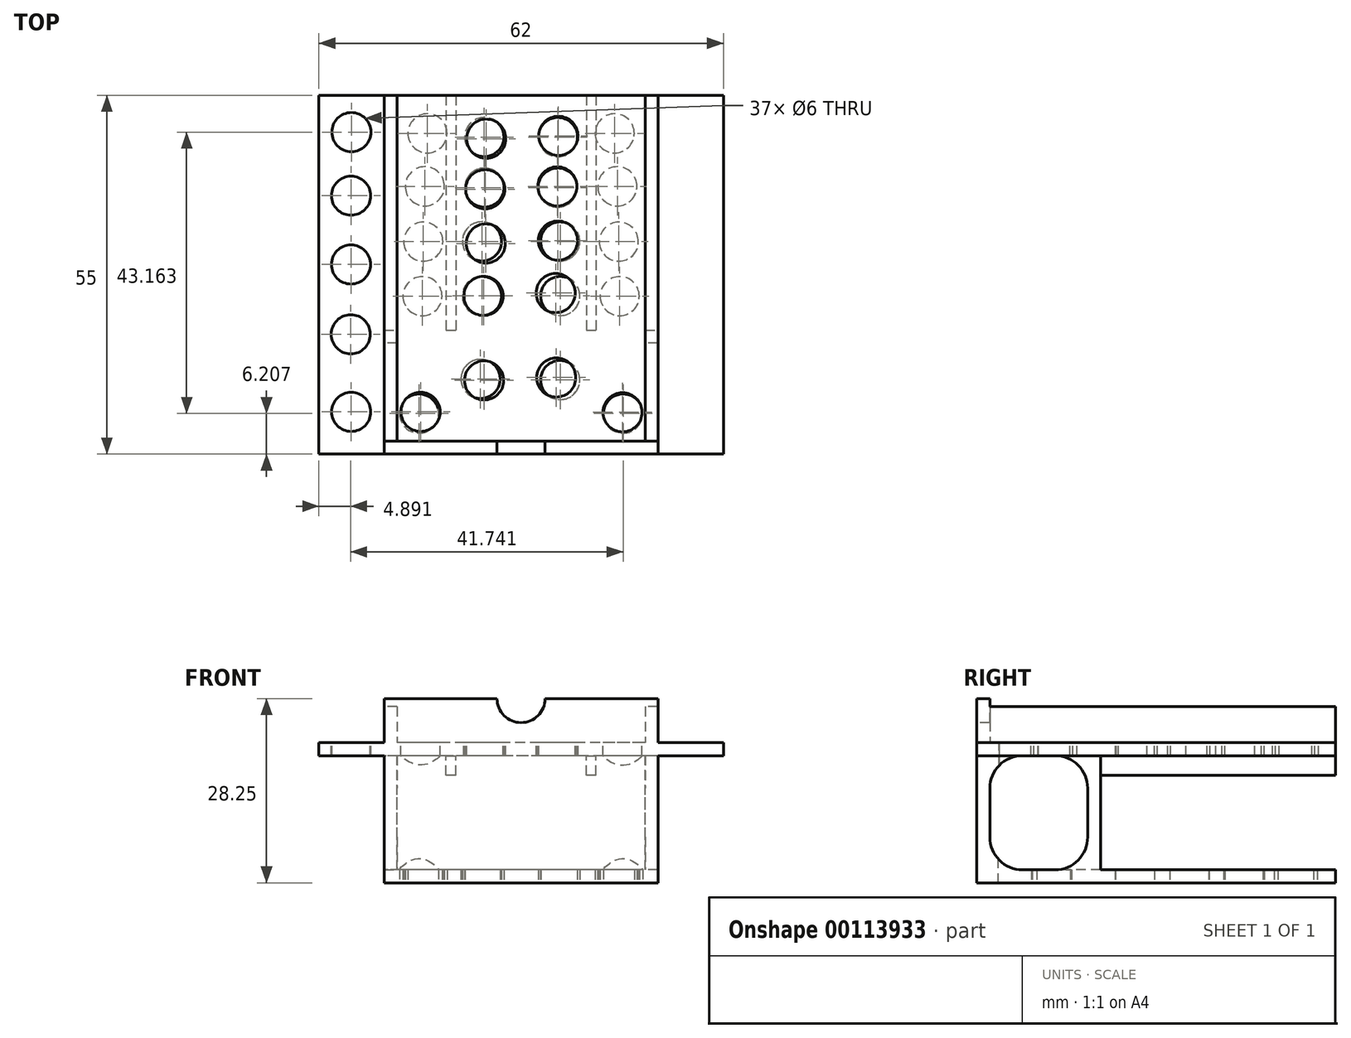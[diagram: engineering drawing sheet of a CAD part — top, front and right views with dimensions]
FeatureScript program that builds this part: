
annotation { "Feature Type Name" : "Feature", "Feature Type Description" : "" }
export const myFeature = defineFeature(function(context is Context, id is Id, definition is map)
    precondition{}
    {
        {
            var Q0;
            Q0=qCreatedBy(makeId("Front.planeOp"),FACE);
            var sketch = newSketch(context, id + "F0", { "sketchPlane" : qUnion([Q0])});
            skLineSegment(sketch, "E0.top", {"start": v(21, 17.5) * mm, "end": v(3.68, 17.5) * mm});
            skLineSegment(sketch, "E0.left", {"start": v(21, -10.75) * mm, "end": v(21, 17.5) * mm});
            skLineSegment(sketch, "E0.right", {"start": v(-21, -10.75) * mm, "end": v(-21, 17.5) * mm});
            skPoint(sketch, "E0.middle", {"position": v(0, 0) * mm});
            skLineSegment(sketch, "E1.bottom", {"start": v(21, -8.75) * mm, "end": v(-21, -8.75) * mm});
            skLineSegment(sketch, "E1.top", {"start": v(21, 8.75) * mm, "end": v(-21, 8.75) * mm});
            skLineSegment(sketch, "E1.left", {"start": v(21, -8.75) * mm, "end": v(21, 8.75) * mm});
            skLineSegment(sketch, "E1.right", {"start": v(-21, -8.75) * mm, "end": v(-21, 8.75) * mm});
            skLineSegment(sketch, "E2.bottom", {"start": v(21, -10.75) * mm, "end": v(-21, -10.75) * mm});
            skLineSegment(sketch, "E2.top", {"start": v(21, 10.75) * mm, "end": v(-21, 10.75) * mm});
            skLineSegment(sketch, "E2.left", {"start": v(21, -10.75) * mm, "end": v(21, 10.75) * mm});
            skLineSegment(sketch, "E2.right", {"start": v(-21, -10.75) * mm, "end": v(-21, 10.75) * mm});
            skArc(sketch, "E3", {"start": v(-3.68, 17.5) * mm, "mid": v(0, 13.82) * mm, "end": v(3.68, 17.5) * mm});
            skLineSegment(sketch, "E4.trimOffspring", {"start": v(-3.68, 17.5) * mm, "end": v(-21, 17.5) * mm});
            skPoint(sketch, "E5.orphan", {"position": v(-21, -17.5) * mm});
            skPoint(sketch, "E6.orphan", {"position": v(21, -17.5) * mm});
            skSolve(sketch);
        }
        {
            var Q0;
            Q0 = qSketchRegion(id + "F0", true);
            extrude(context, id + "F1", {"entities" : qUnion([Q0]), "oppositeDirection" : true, "depth" : 2 * mm});
        }
        {
            var Q0;
            {var subQ0=sQuery(id+"F0.wireOp",EDGE,"E1.top");Q0=makeQuery(id+"F0.imprint","IMPRINT",FACE,{"disambiguationData":[TD([[makeQuery(id+"F0.imprint","IMPRINT",EDGE,{"derivedFrom":subQ0}),-1.0]])]});}
            var Q1;
            {var subQ0=sQuery(id+"F0.wireOp",EDGE,"E1.bottom");Q1=makeQuery(id+"F0.imprint","IMPRINT",FACE,{"disambiguationData":[TD([[makeQuery(id+"F0.imprint","IMPRINT",EDGE,{"derivedFrom":subQ0}),1.0]])]});}
            extrude(context, id + "F2", {"entities" : qUnion([Q0, Q1]), "operationType" : NewBodyOperationType.ADD, "oppositeDirection" : true, "depth" : 55 * mm});
        }
        {
            var Q0;
            Q0=makeQuery(id+"F2.opExtrude","SWEPT_FACE",FACE,{"disambiguationData":[OSD([sQuery(id+"F0.wireOp",EDGE,"E2.top")])]});
            var sketch = newSketch(context, id + "F3", { "sketchPlane" : qUnion([Q0])});
            skLineSegment(sketch, "E7.bottom", {"start": v(21, 2) * mm, "end": v(-21, 2) * mm});
            skLineSegment(sketch, "E7.top", {"start": v(21, 17) * mm, "end": v(-21, 17) * mm});
            skLineSegment(sketch, "E7.left", {"start": v(21, 2) * mm, "end": v(21, 17) * mm});
            skLineSegment(sketch, "E7.right", {"start": v(-21, 2) * mm, "end": v(-21, 17) * mm});
            skPoint(sketch, "E7.middle", {"position": v(0, 9.5) * mm});
            skLineSegment(sketch, "E8", {"start": v(-21, 19) * mm, "end": v(21, 19) * mm});
            skLineSegment(sketch, "E9", {"start": v(0, 55) * mm, "end": v(0, 0) * mm, "construction": true});
            skLineSegment(sketch, "E10", {"start": v(-19, 55) * mm, "end": v(-19, 19) * mm});
            skLineSegment(sketch, "E11.MirrorCS", {"start": v(19, 55) * mm, "end": v(19, 19) * mm});
            skLineSegment(sketch, "E12", {"start": v(-19, 19) * mm, "end": v(-19, 2) * mm});
            skLineSegment(sketch, "E13", {"start": v(19, 19) * mm, "end": v(19, 2) * mm});
            skLineSegment(sketch, "E14.bottom", {"start": v(-11.49, 55) * mm, "end": v(-9.99, 55) * mm});
            skLineSegment(sketch, "E14.top", {"start": v(-11.49, 19) * mm, "end": v(-9.99, 19) * mm});
            skLineSegment(sketch, "E14.left", {"start": v(-11.49, 55) * mm, "end": v(-11.49, 19) * mm});
            skLineSegment(sketch, "E14.right", {"start": v(-9.99, 55) * mm, "end": v(-9.99, 19) * mm});
            skLineSegment(sketch, "E15.MirrorCS", {"start": v(9.99, 55) * mm, "end": v(9.99, 19) * mm});
            skLineSegment(sketch, "E16.MirrorCS", {"start": v(11.49, 55) * mm, "end": v(11.49, 19) * mm});
            skSolve(sketch);
        }
        {
            var Q0;
            {var subQ0=sQuery(id+"F3.wireOp",EDGE,"E7.top");Q0=makeQuery(id+"F3.imprint","IMPRINT",FACE,{"disambiguationData":[TD([[makeQuery(id+"F3.imprint","IMPRINT",EDGE,{"derivedFrom":subQ0}),-1.0]])]});}
            var Q1;
            {var subQ0=sQuery(id+"F3.wireOp",EDGE,"E14.top");Q1=makeQuery(id+"F3.imprint","IMPRINT",FACE,{"disambiguationData":[TD([[makeQuery(id+"F3.imprint","IMPRINT",EDGE,{"derivedFrom":subQ0}),-1.0]])]});}
            extrude(context, id + "F4", {"entities" : qUnion([Q0, Q1]), "operationType" : NewBodyOperationType.ADD, "oppositeDirection" : true, "depth" : 21.48 * mm});
        }
        {
            var Q0;
            {var subQ0=sQuery(id+"F3.wireOp",EDGE,"E7.left");Q0=makeQuery(id+"F3.imprint","IMPRINT",FACE,{"disambiguationData":[TD([[makeQuery(id+"F3.imprint","IMPRINT",EDGE,{"derivedFrom":subQ0}),-1.0]])]});}
            var Q1;
            {var subQ0=sQuery(id+"F3.wireOp",EDGE,"E7.top");var subQ3=sQuery(id+"F3.wireOp",EDGE,"E13");var subQ4=makeQuery(id+"F3.imprint","INTERSECT",VERTEX,{"derivedFrom":[subQ0,subQ3]});Q1=makeQuery(id+"F3.imprint","IMPRINT",FACE,{"disambiguationData":[TD([[makeQuery(id+"F3.imprint","IMPRINT",EDGE,{"disambiguationData":[TD([[subQ4,1.0]])],"derivedFrom":subQ3}),1.0]])]});}
            var Q2;
            {var subQ4=sQuery(id+"F3.wireOp",EDGE,"E11.MirrorCS");Q2=makeQuery(id+"F3.imprint","IMPRINT",FACE,{"disambiguationData":[TD([[makeQuery(id+"F3.imprint","IMPRINT",EDGE,{"derivedFrom":subQ4}),1.0]])]});}
            var Q3;
            {var subQ0=sQuery(id+"F3.wireOp",EDGE,"E7.top");var subQ3=sQuery(id+"F3.wireOp",EDGE,"E12");var subQ4=makeQuery(id+"F3.imprint","INTERSECT",VERTEX,{"derivedFrom":[subQ0,subQ3]});Q3=makeQuery(id+"F3.imprint","IMPRINT",FACE,{"disambiguationData":[TD([[makeQuery(id+"F3.imprint","IMPRINT",EDGE,{"disambiguationData":[TD([[subQ4,1.0]])],"derivedFrom":subQ3}),-1.0]])]});}
            var Q4;
            {var subQ4=sQuery(id+"F3.wireOp",EDGE,"E10");Q4=makeQuery(id+"F3.imprint","IMPRINT",FACE,{"disambiguationData":[TD([[makeQuery(id+"F3.imprint","IMPRINT",EDGE,{"derivedFrom":subQ4}),-1.0]])]});}
            var Q5;
            {var subQ0=sQuery(id+"F3.wireOp",EDGE,"E7.right");Q5=makeQuery(id+"F3.imprint","IMPRINT",FACE,{"disambiguationData":[TD([[makeQuery(id+"F3.imprint","IMPRINT",EDGE,{"derivedFrom":subQ0}),1.0]])]});}
            extrude(context, id + "F5", {"entities" : qUnion([Q0, Q1, Q2, Q3, Q4, Q5]), "operationType" : NewBodyOperationType.ADD, "depth" : 5.5 * mm});
        }
        {
            var Q0;
            Q0=makeQuery(id+"F3.imprint","IMPRINT",FACE,{"disambiguationData":[TD([[makeQuery(id+"F3.imprint","IMPRINT",EDGE,{"derivedFrom":sQuery(id+"F3.wireOp",EDGE,"E14.bottom")}),1.0]])]});
            var Q1;
            {var subQ0=sQuery(id+"F3.wireOp",EDGE,"E15.MirrorCS");Q1=makeQuery(id+"F3.imprint","IMPRINT",FACE,{"disambiguationData":[TD([[makeQuery(id+"F3.imprint","IMPRINT",EDGE,{"derivedFrom":subQ0}),1.0]])]});}
            extrude(context, id + "F6", {"entities" : qUnion([Q0, Q1]), "operationType" : NewBodyOperationType.ADD, "oppositeDirection" : true, "depth" : 5 * mm});
        }
        {
            var Q0;
            {var subQ0=sQuery(id+"F0.wireOp",EDGE,"E2.left");var subQ1=sQuery(id+"F0.wireOp",EDGE,"E2.top");var subQ2=sQuery(id+"F0.wireOp",EDGE,"E0.left");Q0=makeQuery(id+"F5.boolean.opBoolean","MERGE",FACE,{"derivedFrom":[makeQuery(id+"F4.boolean.opBoolean","MERGE",FACE,{"derivedFrom":[makeQuery(id+"F2.boolean.opBoolean","MERGE",FACE,{"derivedFrom":[makeQuery(id+"F1.opExtrude","SWEPT_FACE",FACE,{"disambiguationData":[OSD([subQ2,subQ0])]}),makeQuery(id+"F2.opExtrude","SWEPT_FACE",FACE,{"disambiguationData":[OSD([subQ0]),TDD([makeQuery(id+"F0.imprint","IMPRINT",EDGE,{"disambiguationData":[TD([[makeQuery(id+"F0.imprint","INTERSECT",VERTEX,{"derivedFrom":[sQuery(id+"F0.wireOp",EDGE,"E1.bottom"),subQ0]}),1.0]])],"derivedFrom":subQ0})])]}),makeQuery(id+"F2.opExtrude","SWEPT_FACE",FACE,{"disambiguationData":[OSD([subQ0]),TDD([makeQuery(id+"F0.imprint","IMPRINT",EDGE,{"disambiguationData":[TD([[makeQuery(id+"F0.imprint","INTERSECT",VERTEX,{"derivedFrom":[sQuery(id+"F0.wireOp",EDGE,"E1.top"),subQ0]}),-1.0]])],"derivedFrom":subQ0})])]})]}),makeQuery(id+"F4.opExtrude","SWEPT_FACE",FACE,{"disambiguationData":[OSD([subQ2,subQ1,subQ0])]})]}),makeQuery(id+"F5.opExtrude","SWEPT_FACE",FACE,{"disambiguationData":[OSD([subQ2,subQ1,subQ0,sQuery(id+"F3.wireOp",EDGE,"E7.left")])]})]});}
            var sketch = newSketch(context, id + "F7", { "sketchPlane" : qUnion([Q0])});
            skLineSegment(sketch, "E17", {"start": v(55, 8.75) * mm, "end": v(0, 8.75) * mm});
            skPoint(sketch, "E17.endSnap0", {"position": v(9.5, 8.75) * mm});
            skLineSegment(sketch, "E18", {"start": v(0, 8.75) * mm, "end": v(0, 11) * mm});
            skLineSegment(sketch, "E19", {"start": v(55, 8.75) * mm, "end": v(0.94, 8.75) * mm});
            skLineSegment(sketch, "E20", {"start": v(55, 10.75) * mm, "end": v(0, 10.75) * mm});
            skLineSegment(sketch, "E21", {"start": v(0, 10.75) * mm, "end": v(0, 8.75) * mm});
            skLineSegment(sketch, "E22", {"start": v(55, 8.75) * mm, "end": v(55, 10.75) * mm});
            skSolve(sketch);
        }
        {
            var Q0;
            {var subQ7=sQuery(id+"F7.wireOp",EDGE,"E17");Q0=makeQuery(id+"F7.imprint","IMPRINT",FACE,{"disambiguationData":[TD([[makeQuery(id+"F7.imprint","IMPRINT",EDGE,{"derivedFrom":subQ7}),-1.0]])]});}
            extrude(context, id + "F8", {"entities" : qUnion([Q0]), "operationType" : NewBodyOperationType.ADD, "depth" : 10 * mm});
        }
        {
            var Q0;
            {var subQ0=sQuery(id+"F0.wireOp",EDGE,"E2.right");var subQ1=sQuery(id+"F0.wireOp",EDGE,"E2.top");var subQ2=sQuery(id+"F0.wireOp",EDGE,"E0.right");Q0=makeQuery(id+"F5.boolean.opBoolean","MERGE",FACE,{"derivedFrom":[makeQuery(id+"F4.boolean.opBoolean","MERGE",FACE,{"derivedFrom":[makeQuery(id+"F2.boolean.opBoolean","MERGE",FACE,{"derivedFrom":[makeQuery(id+"F1.opExtrude","SWEPT_FACE",FACE,{"disambiguationData":[OSD([subQ2,subQ0])]}),makeQuery(id+"F2.opExtrude","SWEPT_FACE",FACE,{"disambiguationData":[OSD([subQ0]),TDD([makeQuery(id+"F0.imprint","IMPRINT",EDGE,{"disambiguationData":[TD([[makeQuery(id+"F0.imprint","INTERSECT",VERTEX,{"derivedFrom":[sQuery(id+"F0.wireOp",EDGE,"E1.bottom"),subQ0]}),1.0]])],"derivedFrom":subQ0})])]}),makeQuery(id+"F2.opExtrude","SWEPT_FACE",FACE,{"disambiguationData":[OSD([subQ0]),TDD([makeQuery(id+"F0.imprint","IMPRINT",EDGE,{"disambiguationData":[TD([[makeQuery(id+"F0.imprint","INTERSECT",VERTEX,{"derivedFrom":[sQuery(id+"F0.wireOp",EDGE,"E1.top"),subQ0]}),-1.0]])],"derivedFrom":subQ0})])]})]}),makeQuery(id+"F4.opExtrude","SWEPT_FACE",FACE,{"disambiguationData":[OSD([subQ2,subQ1,subQ0])]})]}),makeQuery(id+"F5.opExtrude","SWEPT_FACE",FACE,{"disambiguationData":[OSD([subQ2,subQ1,subQ0,sQuery(id+"F3.wireOp",EDGE,"E7.right")])]})]});}
            var sketch = newSketch(context, id + "F9", { "sketchPlane" : qUnion([Q0])});
            skLineSegment(sketch, "E23", {"start": v(0, 10.75) * mm, "end": v(-55, 10.75) * mm});
            skLineSegment(sketch, "E24", {"start": v(-55, 10.75) * mm, "end": v(-55, 8.75) * mm});
            skLineSegment(sketch, "E25", {"start": v(-55, 8.75) * mm, "end": v(0, 8.75) * mm});
            skLineSegment(sketch, "E26", {"start": v(0, 8.75) * mm, "end": v(0, 10.75) * mm});
            skSolve(sketch);
        }
        {
            var Q0;
            Q0=makeQuery(id+"F9.imprint","IMPRINT",FACE,{"disambiguationData":[TD([[makeQuery(id+"F9.imprint","IMPRINT",EDGE,{"derivedFrom":sQuery(id+"F9.wireOp",EDGE,"E23")}),1.0]])]});
            extrude(context, id + "F10", {"entities" : qUnion([Q0]), "operationType" : NewBodyOperationType.ADD, "depth" : 10 * mm});
        }
        {
            var Q0;
            Q0=makeQuery(id+"F10.opExtrude","SWEPT_FACE",FACE,{"disambiguationData":[OSD([sQuery(id+"F9.wireOp",EDGE,"E23")])]});
            var sketch = newSketch(context, id + "F11", { "sketchPlane" : qUnion([Q0])});
            skLineSegment(sketch, "E27", {"start": v(-26, 55) * mm, "end": v(-26, 0) * mm, "construction": true});
            skCircle(sketch, "E28", {"center": v(-26, 49.37) * mm, "radius": 3 * mm});
            skCircle(sketch, "E29", {"center": v(-26.06, 39.62) * mm, "radius": 3 * mm});
            skCircle(sketch, "E30", {"center": v(-26.07, 29.07) * mm, "radius": 3 * mm});
            skCircle(sketch, "E31", {"center": v(-26.1, 18.36) * mm, "radius": 3 * mm});
            skCircle(sketch, "E32", {"center": v(-26.05, 6.47) * mm, "radius": 3 * mm});
            skCircle(sketch, "E33.MirrorC", {"center": v(26.05, 6.47) * mm, "radius": 3 * mm});
            skCircle(sketch, "E34.MirrorC", {"center": v(26.1, 18.36) * mm, "radius": 3 * mm});
            skCircle(sketch, "E35.MirrorC", {"center": v(26.07, 29.07) * mm, "radius": 3 * mm});
            skCircle(sketch, "E36.MirrorC", {"center": v(26.06, 39.62) * mm, "radius": 3 * mm});
            skCircle(sketch, "E37.MirrorC", {"center": v(26, 49.37) * mm, "radius": 3 * mm});
            skSolve(sketch);
        }
        {
            var Q0;
            Q0=makeQuery(id+"F11.imprint","IMPRINT",FACE,{"disambiguationData":[TD([[makeQuery(id+"F11.imprint","IMPRINT",EDGE,{"derivedFrom":sQuery(id+"F11.wireOp",EDGE,"E33.MirrorC")}),-1.0]])]});
            var Q1;
            Q1=makeQuery(id+"F11.imprint","IMPRINT",FACE,{"disambiguationData":[TD([[makeQuery(id+"F11.imprint","IMPRINT",EDGE,{"derivedFrom":sQuery(id+"F11.wireOp",EDGE,"E34.MirrorC")}),-1.0]])]});
            var Q2;
            Q2=makeQuery(id+"F11.imprint","IMPRINT",FACE,{"disambiguationData":[TD([[makeQuery(id+"F11.imprint","IMPRINT",EDGE,{"derivedFrom":sQuery(id+"F11.wireOp",EDGE,"E35.MirrorC")}),-1.0]])]});
            var Q3;
            Q3=makeQuery(id+"F11.imprint","IMPRINT",FACE,{"disambiguationData":[TD([[makeQuery(id+"F11.imprint","IMPRINT",EDGE,{"derivedFrom":sQuery(id+"F11.wireOp",EDGE,"E36.MirrorC")}),-1.0]])]});
            var Q4;
            Q4=makeQuery(id+"F11.imprint","IMPRINT",FACE,{"disambiguationData":[TD([[makeQuery(id+"F11.imprint","IMPRINT",EDGE,{"derivedFrom":sQuery(id+"F11.wireOp",EDGE,"E37.MirrorC")}),-1.0]])]});
            var Q5;
            Q5=makeQuery(id+"F11.imprint","IMPRINT",FACE,{"disambiguationData":[TD([[makeQuery(id+"F11.imprint","IMPRINT",EDGE,{"derivedFrom":sQuery(id+"F11.wireOp",EDGE,"E28")}),1.0]])]});
            var Q6;
            Q6=makeQuery(id+"F11.imprint","IMPRINT",FACE,{"disambiguationData":[TD([[makeQuery(id+"F11.imprint","IMPRINT",EDGE,{"derivedFrom":sQuery(id+"F11.wireOp",EDGE,"E32")}),1.0]])]});
            var Q7;
            Q7=makeQuery(id+"F11.imprint","IMPRINT",FACE,{"disambiguationData":[TD([[makeQuery(id+"F11.imprint","IMPRINT",EDGE,{"derivedFrom":sQuery(id+"F11.wireOp",EDGE,"E31")}),1.0]])]});
            var Q8;
            Q8=makeQuery(id+"F11.imprint","IMPRINT",FACE,{"disambiguationData":[TD([[makeQuery(id+"F11.imprint","IMPRINT",EDGE,{"derivedFrom":sQuery(id+"F11.wireOp",EDGE,"E30")}),1.0]])]});
            var Q9;
            Q9=makeQuery(id+"F11.imprint","IMPRINT",FACE,{"disambiguationData":[TD([[makeQuery(id+"F11.imprint","IMPRINT",EDGE,{"derivedFrom":sQuery(id+"F11.wireOp",EDGE,"E29")}),1.0]])]});
            extrude(context, id + "F12", {"entities" : qUnion([Q0, Q1, Q2, Q3, Q4, Q5, Q6, Q7, Q8, Q9]), "operationType" : NewBodyOperationType.REMOVE, "oppositeDirection" : true, "depth" : 25 * mm});
        }
        {
            var Q0;
            {var subQ2=sQuery(id+"F0.wireOp",EDGE,"E2.bottom");Q0=makeQuery(id+"F4.boolean.opBoolean","SPLIT",FACE,{"disambiguationData":[TD([makeQuery(id+"F4.opExtrude","SWEPT_FACE",FACE,{"disambiguationData":[OSD([sQuery(id+"F3.wireOp",EDGE,"E8"),sQuery(id+"F3.wireOp",EDGE,"E14.top")])]})])],"derivedFrom":makeQuery(id+"F2.opExtrude","SWEPT_FACE",FACE,{"disambiguationData":[OSD([subQ2])]})});}
            var sketch = newSketch(context, id + "F13", { "sketchPlane" : qUnion([Q0])});
            skCircle(sketch, "E38", {"center": v(-15.12, -24.2) * mm, "radius": 3 * mm});
            skCircle(sketch, "E39", {"center": v(-6, -24.24) * mm, "radius": 3 * mm});
            skCircle(sketch, "E40", {"center": v(-14.98, -32.58) * mm, "radius": 3 * mm});
            skCircle(sketch, "E41", {"center": v(-6, -32.6) * mm, "radius": 3 * mm});
            skCircle(sketch, "E42", {"center": v(-5.62, -40.86) * mm, "radius": 3 * mm});
            skCircle(sketch, "E43", {"center": v(-14.75, -41.06) * mm, "radius": 3 * mm});
            skCircle(sketch, "E44", {"center": v(-14.35, -49.18) * mm, "radius": 3 * mm});
            skCircle(sketch, "E45", {"center": v(-5.65, -48.61) * mm, "radius": 3 * mm});
            skCircle(sketch, "E46", {"center": v(-15.63, -6.2) * mm, "radius": 3 * mm});
            skLineSegment(sketch, "E47", {"start": v(0, 29.9) * mm, "end": v(0, -70.72) * mm, "construction": true});
            skCircle(sketch, "E48.MirrorC", {"center": v(5.65, -48.61) * mm, "radius": 3 * mm});
            skCircle(sketch, "E49.MirrorC", {"center": v(14.35, -49.18) * mm, "radius": 3 * mm});
            skCircle(sketch, "E50.MirrorC", {"center": v(14.75, -41.06) * mm, "radius": 3 * mm});
            skCircle(sketch, "E51.MirrorC", {"center": v(5.62, -40.86) * mm, "radius": 3 * mm});
            skCircle(sketch, "E52.MirrorC", {"center": v(6, -32.6) * mm, "radius": 3 * mm});
            skCircle(sketch, "E53.MirrorC", {"center": v(14.98, -32.58) * mm, "radius": 3 * mm});
            skCircle(sketch, "E54.MirrorC", {"center": v(15.12, -24.2) * mm, "radius": 3 * mm});
            skCircle(sketch, "E55.MirrorC", {"center": v(6, -24.24) * mm, "radius": 3 * mm});
            skCircle(sketch, "E56.MirrorC", {"center": v(15.63, -6.2) * mm, "radius": 3 * mm});
            skCircle(sketch, "E57", {"center": v(-6.21, -11.52) * mm, "radius": 3 * mm});
            skCircle(sketch, "E58", {"center": v(6, -11.35) * mm, "radius": 3 * mm});
            skSolve(sketch);
        }
        {
            var Q0;
            Q0 = qSketchRegion(id + "F13", true);
            extrude(context, id + "F14", {"entities" : qUnion([Q0]), "operationType" : NewBodyOperationType.REMOVE, "oppositeDirection" : true, "depth" : 10 * mm});
        }
        {
            var Q0;
            {var subQ0=sQuery(id+"F3.wireOp",EDGE,"E14.right");Q0=makeQuery(id+"F3.imprint","IMPRINT",FACE,{"disambiguationData":[TD([[makeQuery(id+"F3.imprint","IMPRINT",EDGE,{"derivedFrom":subQ0}),1.0]])]});}
            var sketch = newSketch(context, id + "F15", { "sketchPlane" : qUnion([Q0])});
            skCircle(sketch, "E59", {"center": v(5.72, 48.8) * mm, "radius": 3 * mm});
            skCircle(sketch, "E60", {"center": v(-5.35, 48.36) * mm, "radius": 3 * mm});
            skCircle(sketch, "E61", {"center": v(5.56, 41.05) * mm, "radius": 3 * mm});
            skCircle(sketch, "E62", {"center": v(-5.5, 40.6) * mm, "radius": 3 * mm});
            skCircle(sketch, "E63", {"center": v(5.65, 32.74) * mm, "radius": 3 * mm});
            skCircle(sketch, "E64", {"center": v(-5.41, 32.3) * mm, "radius": 3 * mm});
            skCircle(sketch, "E65", {"center": v(5.3, 24.69) * mm, "radius": 3 * mm});
            skCircle(sketch, "E66", {"center": v(-5.76, 24.24) * mm, "radius": 3 * mm});
            skCircle(sketch, "E67", {"center": v(5.39, 11.73) * mm, "radius": 3 * mm});
            skCircle(sketch, "E68", {"center": v(-5.67, 11.29) * mm, "radius": 3 * mm});
            skCircle(sketch, "E69", {"center": v(-15.4, 6.47) * mm, "radius": 3 * mm});
            skCircle(sketch, "E70", {"center": v(15.54, 6.4) * mm, "radius": 3 * mm});
            skSolve(sketch);
        }
        {
            var Q0;
            Q0 = qSketchRegion(id + "F15", true);
            extrude(context, id + "F16", {"entities" : qUnion([Q0]), "operationType" : NewBodyOperationType.REMOVE, "oppositeDirection" : true, "depth" : 10 * mm});
        }
        {
            var Q0;
            Q0=makeQuery(id+"F4.boolean.opBoolean","INTERSECT",EDGE,{"derivedFrom":[makeQuery(id+"F2.opExtrude","SWEPT_FACE",FACE,{"disambiguationData":[OSD([sQuery(id+"F0.wireOp",EDGE,"E1.bottom")])]}),makeQuery(id+"F4.opExtrude","SWEPT_FACE",FACE,{"disambiguationData":[OSD([sQuery(id+"F3.wireOp",EDGE,"E7.top")])]})]});
            var Q1;
            Q1=makeQuery(id+"F2.boolean.opBoolean","INTERSECT",EDGE,{"derivedFrom":[makeQuery(id+"F1.opExtrude","CAP_FACE",FACE,{"disambiguationData":[OSD([sQuery(id+"F0.wireOp",EDGE,"E0.bottom"),sQuery(id+"F0.wireOp",EDGE,"E0.top"),sQuery(id+"F0.wireOp",EDGE,"E0.left"),sQuery(id+"F0.wireOp",EDGE,"E0.right"),sQuery(id+"F0.wireOp",EDGE,"E2.left"),sQuery(id+"F0.wireOp",EDGE,"E2.right"),sQuery(id+"F0.wireOp",EDGE,"E3"),sQuery(id+"F0.wireOp",EDGE,"E4.trimOffspring")])],"isStart":false}),makeQuery(id+"F2.opExtrude","SWEPT_FACE",FACE,{"disambiguationData":[OSD([sQuery(id+"F0.wireOp",EDGE,"E1.bottom")])]})]});
            var Q2;
            Q2=makeQuery(id+"F4.boolean.opBoolean","INTERSECT",EDGE,{"derivedFrom":[makeQuery(id+"F2.opExtrude","SWEPT_FACE",FACE,{"disambiguationData":[OSD([sQuery(id+"F0.wireOp",EDGE,"E1.top")])]}),makeQuery(id+"F4.opExtrude","SWEPT_FACE",FACE,{"disambiguationData":[OSD([sQuery(id+"F3.wireOp",EDGE,"E7.top")])]})]});
            var Q3;
            Q3=makeQuery(id+"F2.boolean.opBoolean","INTERSECT",EDGE,{"derivedFrom":[makeQuery(id+"F1.opExtrude","CAP_FACE",FACE,{"disambiguationData":[OSD([sQuery(id+"F0.wireOp",EDGE,"E0.bottom"),sQuery(id+"F0.wireOp",EDGE,"E0.top"),sQuery(id+"F0.wireOp",EDGE,"E0.left"),sQuery(id+"F0.wireOp",EDGE,"E0.right"),sQuery(id+"F0.wireOp",EDGE,"E2.left"),sQuery(id+"F0.wireOp",EDGE,"E2.right"),sQuery(id+"F0.wireOp",EDGE,"E3"),sQuery(id+"F0.wireOp",EDGE,"E4.trimOffspring")])],"isStart":false}),makeQuery(id+"F2.opExtrude","SWEPT_FACE",FACE,{"disambiguationData":[OSD([sQuery(id+"F0.wireOp",EDGE,"E1.top")])]})]});
            fillet(context, id + "F17", {"entities" : qUnion([Q0, Q1, Q2, Q3]), "radius" : 5 * mm, "tangentPropagation" : true, "allowEdgeOverflow" : false});
        }
    });
